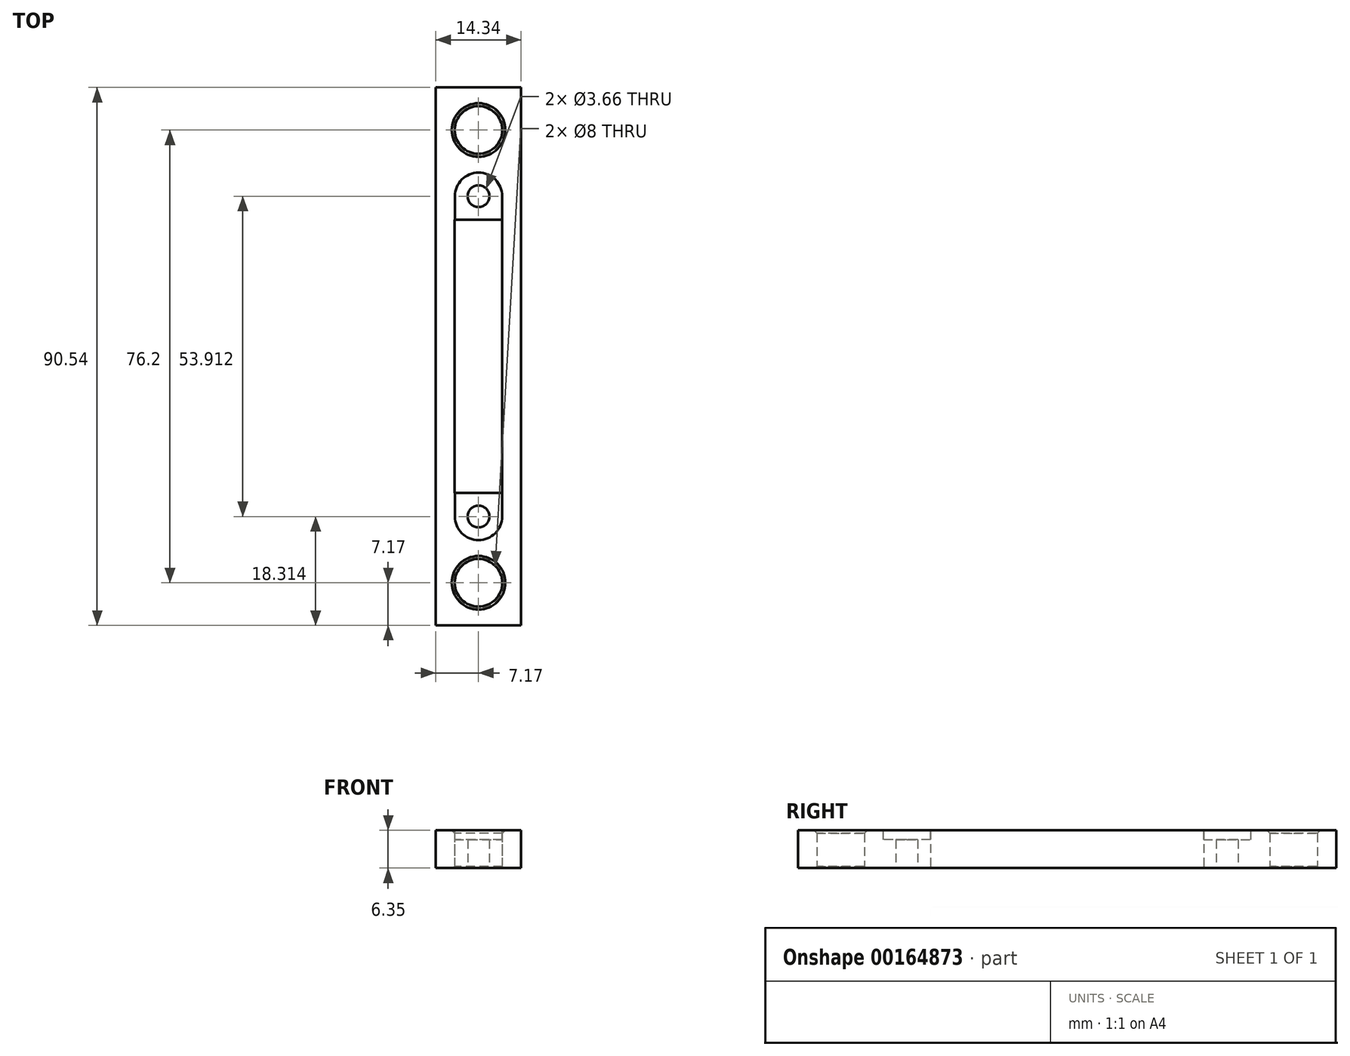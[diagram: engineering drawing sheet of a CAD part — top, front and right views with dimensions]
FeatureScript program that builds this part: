
annotation { "Feature Type Name" : "Feature", "Feature Type Description" : "" }
export const myFeature = defineFeature(function(context is Context, id is Id, definition is map)
    precondition{}
    {
        {
            var Q0;
            Q0=qCreatedBy(makeId("Top.planeOp"),FACE);
            var sketch = newSketch(context, id + "F0", { "sketchPlane" : qUnion([Q0])});
            skLineSegment(sketch, "E0.bottom", {"start": v(4, 22.99) * mm, "end": v(-4, 22.99) * mm});
            skLineSegment(sketch, "E0.top", {"start": v(4, -22.99) * mm, "end": v(-4, -22.99) * mm});
            skLineSegment(sketch, "E0.left", {"start": v(4, 22.99) * mm, "end": v(4, -22.99) * mm});
            skLineSegment(sketch, "E0.right", {"start": v(-4, 22.99) * mm, "end": v(-4, -22.99) * mm});
            skPoint(sketch, "E0.middle", {"position": v(0, 0) * mm});
            skLineSegment(sketch, "E1.bottom", {"start": v(7.17, 45.27) * mm, "end": v(-7.18, 45.27) * mm});
            skLineSegment(sketch, "E1.top", {"start": v(7.17, -45.27) * mm, "end": v(-7.18, -45.27) * mm});
            skLineSegment(sketch, "E1.left", {"start": v(7.18, 45.27) * mm, "end": v(7.18, -45.27) * mm});
            skLineSegment(sketch, "E1.right", {"start": v(-7.18, 45.27) * mm, "end": v(-7.18, -45.27) * mm});
            skLineSegment(sketch, "E2", {"start": v(0, 22.99) * mm, "end": v(0, 26.96) * mm, "construction": true});
            skLineSegment(sketch, "E3", {"start": v(0, 26.96) * mm, "end": v(0, 38.1) * mm, "construction": true});
            skLineSegment(sketch, "E4", {"start": v(4, 0) * mm, "end": v(7.18, 0) * mm, "construction": true});
            skLineSegment(sketch, "E5", {"start": v(0, -22.99) * mm, "end": v(0, -26.96) * mm, "construction": true});
            skLineSegment(sketch, "E6", {"start": v(0, -26.96) * mm, "end": v(0, -38.1) * mm, "construction": true});
            skCircle(sketch, "E7", {"center": v(0, 26.96) * mm, "radius": 1.83 * mm});
            skCircle(sketch, "E8", {"center": v(0, 38.1) * mm, "radius": 4 * mm});
            skCircle(sketch, "E9", {"center": v(0, -38.1) * mm, "radius": 4 * mm});
            skCircle(sketch, "E10", {"center": v(0, -26.96) * mm, "radius": 1.83 * mm});
            skCircle(sketch, "E11", {"center": v(0, 26.96) * mm, "radius": 3.97 * mm, "construction": true});
            skCircle(sketch, "E12", {"center": v(0, 38.1) * mm, "radius": 7.18 * mm, "construction": true});
            skSolve(sketch);
        }
        {
            var Q0;
            Q0=qSketchRegion(id+"F0",true);
            extrude(context, id + "F1", {"entities" : qUnion([Q0]), "depth" : 6.35 * mm});
        }
        {
            var Q0;
            Q0=makeQuery(id+"F1.opExtrude","CAP_EDGE",EDGE,{"disambiguationData":[OSD([sQuery(id+"F0.wireOp",EDGE,"E8")])],"isStart":true});
            var Q1;
            Q1=makeQuery(id+"F1.opExtrude","CAP_EDGE",EDGE,{"disambiguationData":[OSD([sQuery(id+"F0.wireOp",EDGE,"E9")])],"isStart":true});
            chamfer(context, id + "F2", {"entities" : qUnion([Q0, Q1]), "width" : 0.25 * mm, "tangentPropagation" : true});
        }
        {
            var Q0;
            Q0=makeQuery(id+"F1.opExtrude","CAP_FACE",FACE,{"disambiguationData":[OSD([sQuery(id+"F0.wireOp",EDGE,"E0.bottom"),sQuery(id+"F0.wireOp",EDGE,"E0.top"),sQuery(id+"F0.wireOp",EDGE,"E0.left"),sQuery(id+"F0.wireOp",EDGE,"E0.right"),sQuery(id+"F0.wireOp",EDGE,"E1.bottom"),sQuery(id+"F0.wireOp",EDGE,"E1.top"),sQuery(id+"F0.wireOp",EDGE,"E1.left"),sQuery(id+"F0.wireOp",EDGE,"E1.right"),sQuery(id+"F0.wireOp",EDGE,"E7"),sQuery(id+"F0.wireOp",EDGE,"E8"),sQuery(id+"F0.wireOp",EDGE,"E9"),sQuery(id+"F0.wireOp",EDGE,"E10")])],"isStart":false});
            var sketch = newSketch(context, id + "F3", { "sketchPlane" : qUnion([Q0])});
            skLineSegment(sketch, "E13.bottom", {"start": v(3.97, 22.99) * mm, "end": v(-3.97, 22.99) * mm});
            skLineSegment(sketch, "E13.top", {"start": v(3.97, 30.92) * mm, "end": v(-3.97, 30.92) * mm});
            skLineSegment(sketch, "E13.left", {"start": v(3.97, 22.99) * mm, "end": v(3.97, 30.92) * mm});
            skLineSegment(sketch, "E13.right", {"start": v(-3.97, 22.99) * mm, "end": v(-3.97, 30.92) * mm});
            skPoint(sketch, "E13.middle", {"position": v(0, 26.96) * mm});
            skLineSegment(sketch, "E14.bottom", {"start": v(3.97, -22.99) * mm, "end": v(-3.97, -22.99) * mm});
            skLineSegment(sketch, "E14.top", {"start": v(3.97, -30.92) * mm, "end": v(-3.97, -30.92) * mm});
            skLineSegment(sketch, "E14.left", {"start": v(3.97, -22.99) * mm, "end": v(3.97, -30.92) * mm});
            skLineSegment(sketch, "E14.right", {"start": v(-3.97, -22.99) * mm, "end": v(-3.97, -30.92) * mm});
            skPoint(sketch, "E14.middle", {"position": v(0, -26.96) * mm});
            skSolve(sketch);
        }
        {
            var Q0;
            Q0 = qSketchRegion(id + "F3", true);
            extrude(context, id + "F4", {"entities" : qUnion([Q0]), "operationType" : NewBodyOperationType.REMOVE, "oppositeDirection" : true, "depth" : 1.59 * mm});
        }
        {
            var Q0;
            Q0=makeQuery(id+"F4.boolean.opBoolean","COPY",EDGE,{"derivedFrom":makeQuery(id+"F4.opExtrude","SWEPT_EDGE",EDGE,{"disambiguationData":[OSD([sQuery(id+"F3.wireOp",EDGE,"E14.top"),sQuery(id+"F3.wireOp",EDGE,"E14.right")])]})});
            var Q1;
            Q1=makeQuery(id+"F4.boolean.opBoolean","COPY",EDGE,{"derivedFrom":makeQuery(id+"F4.opExtrude","SWEPT_EDGE",EDGE,{"disambiguationData":[OSD([sQuery(id+"F3.wireOp",EDGE,"E14.top"),sQuery(id+"F3.wireOp",EDGE,"E14.left")])]})});
            var Q2;
            Q2=makeQuery(id+"F4.boolean.opBoolean","COPY",EDGE,{"derivedFrom":makeQuery(id+"F4.opExtrude","SWEPT_EDGE",EDGE,{"disambiguationData":[OSD([sQuery(id+"F3.wireOp",EDGE,"E13.top"),sQuery(id+"F3.wireOp",EDGE,"E13.right")])]})});
            var Q3;
            Q3=makeQuery(id+"F4.boolean.opBoolean","COPY",EDGE,{"derivedFrom":makeQuery(id+"F4.opExtrude","SWEPT_EDGE",EDGE,{"disambiguationData":[OSD([sQuery(id+"F3.wireOp",EDGE,"E13.top"),sQuery(id+"F3.wireOp",EDGE,"E13.left")])]})});
            fillet(context, id + "F5", {"entities" : qUnion([Q0, Q1, Q2, Q3]), "radius" : 3.97 * mm, "tangentPropagation" : true, "allowEdgeOverflow" : false});
        }
        {
            var Q0;
            Q0=makeQuery(id+"F1.opExtrude","CAP_EDGE",EDGE,{"disambiguationData":[OSD([sQuery(id+"F0.wireOp",EDGE,"E8")])],"isStart":false});
            var Q1;
            Q1=makeQuery(id+"F1.opExtrude","CAP_EDGE",EDGE,{"disambiguationData":[OSD([sQuery(id+"F0.wireOp",EDGE,"E9")])],"isStart":false});
            chamfer(context, id + "F6", {"entities" : qUnion([Q0, Q1]), "width" : 0.5 * mm, "tangentPropagation" : true});
        }
    });
